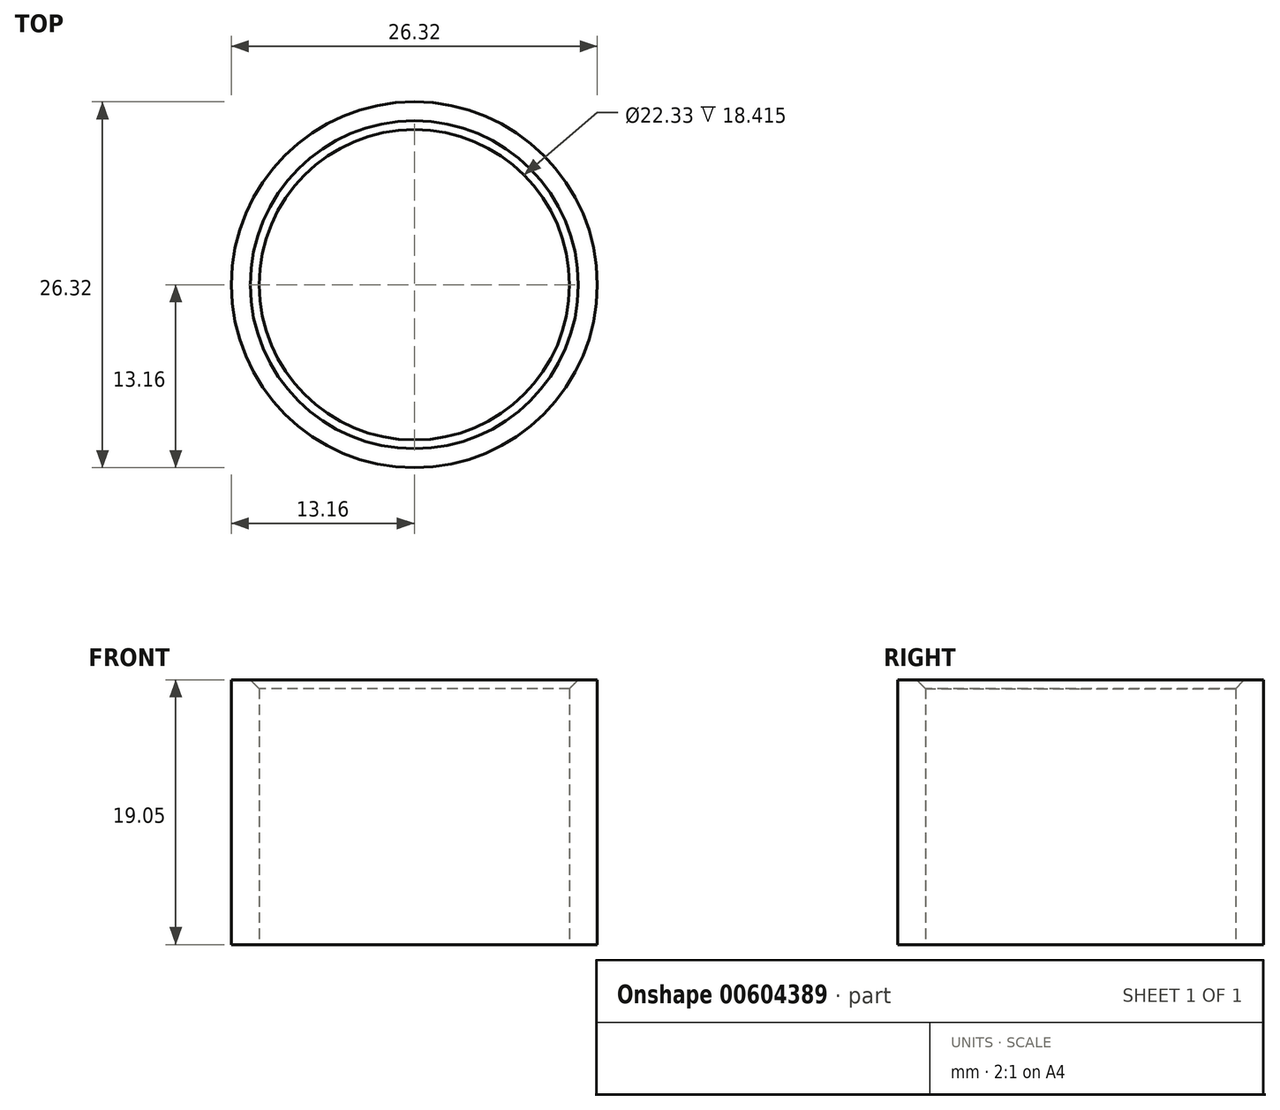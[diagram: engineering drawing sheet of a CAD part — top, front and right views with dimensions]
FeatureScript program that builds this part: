
annotation { "Feature Type Name" : "Feature", "Feature Type Description" : "" }
export const myFeature = defineFeature(function(context is Context, id is Id, definition is map)
    precondition{}
    {
        {
            var Q0;
            Q0=qCreatedBy(makeId("Top.planeOp"),FACE);
            var sketch = newSketch(context, id + "F0", { "sketchPlane" : qUnion([Q0])});
            skCircle(sketch, "E0", {"center": v(0, 0) * mm, "radius": 11.11 * mm});
            skCircle(sketch, "E1.0", {"center": v(0, 0) * mm, "radius": 11.16 * mm});
            skCircle(sketch, "E2.0", {"center": v(0, 0) * mm, "radius": 13.16 * mm});
            skSolve(sketch);
        }
        {
            var Q0;
            Q0=makeQuery(id+"F0.imprint","IMPRINT",FACE,{"disambiguationData":[TD([[makeQuery(id+"F0.imprint","IMPRINT",EDGE,{"derivedFrom":sQuery(id+"F0.wireOp",EDGE,"E1.0")}),-1.0]])]});
            extrude(context, id + "F1", {"entities" : qUnion([Q0]), "depth" : 19.05 * mm, "offsetDistance" : 25.4 * mm});
        }
        {
            var Q0;
            Q0=makeQuery(id+"F1.opExtrude","CAP_EDGE",EDGE,{"disambiguationData":[OSD([sQuery(id+"F0.wireOp",EDGE,"E1.0")])],"isStart":false});
            chamfer(context, id + "F2", {"entities" : qUnion([Q0]), "width" : 0.64 * mm, "tangentPropagation" : true});
        }
    });
